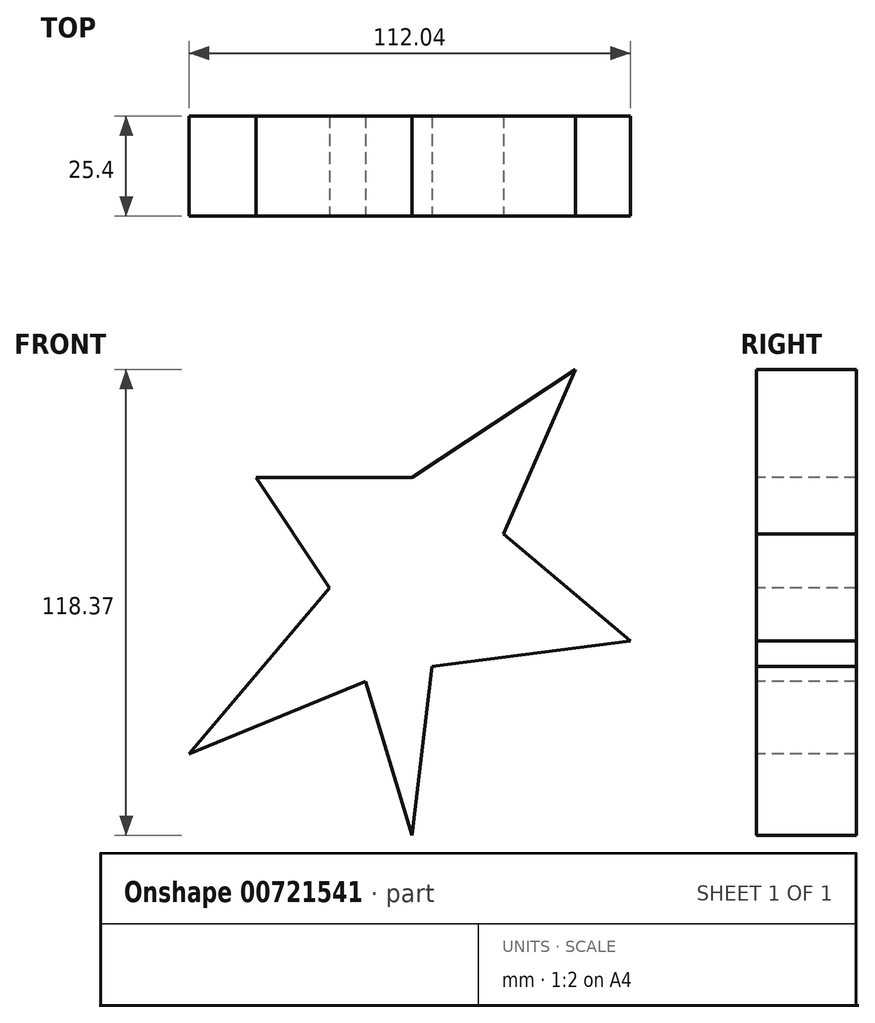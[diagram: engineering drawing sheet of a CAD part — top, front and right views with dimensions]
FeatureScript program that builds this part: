
annotation { "Feature Type Name" : "Feature", "Feature Type Description" : "" }
export const myFeature = defineFeature(function(context is Context, id is Id, definition is map)
    precondition{}
    {
        {
            var Q0;
            Q0=qCreatedBy(makeId("Front.planeOp"),FACE);
            var sketch = newSketch(context, id + "F0", { "sketchPlane" : qUnion([Q0])});
            skLineSegment(sketch, "E0", {"start": v(0, 0) * mm, "end": v(5.04, 43) * mm});
            skLineSegment(sketch, "E1", {"start": v(5.04, 43) * mm, "end": v(55.47, 49.39) * mm});
            skLineSegment(sketch, "E2", {"start": v(55.47, 49.39) * mm, "end": v(23.3, 76.6) * mm});
            skLineSegment(sketch, "E3", {"start": v(23.3, 76.6) * mm, "end": v(41.54, 118.37) * mm});
            skLineSegment(sketch, "E4", {"start": v(41.54, 118.37) * mm, "end": v(0, 90.94) * mm});
            skLineSegment(sketch, "E5", {"start": v(0, 90.94) * mm, "end": v(-39.62, 90.94) * mm});
            skLineSegment(sketch, "E6", {"start": v(-39.62, 90.94) * mm, "end": v(-20.9, 62.88) * mm});
            skLineSegment(sketch, "E7", {"start": v(-20.9, 62.88) * mm, "end": v(-56.57, 20.7) * mm});
            skLineSegment(sketch, "E8", {"start": v(-56.57, 20.7) * mm, "end": v(-11.77, 39.1) * mm});
            skLineSegment(sketch, "E9", {"start": v(-11.77, 39.1) * mm, "end": v(0, 0) * mm});
            skSolve(sketch);
        }
        {
            var Q0;
            Q0=makeQuery(id+"F0.imprint","IMPRINT",FACE,{"disambiguationData":[TD([[makeQuery(id+"F0.imprint","IMPRINT",EDGE,{"derivedFrom":sQuery(id+"F0.wireOp",EDGE,"E0")}),1.0]])]});
            extrude(context, id + "F1", {"entities" : qUnion([Q0]), "oppositeDirection" : true, "depth" : 25.4 * mm, "offsetDistance" : 25.4 * mm});
        }
    });
